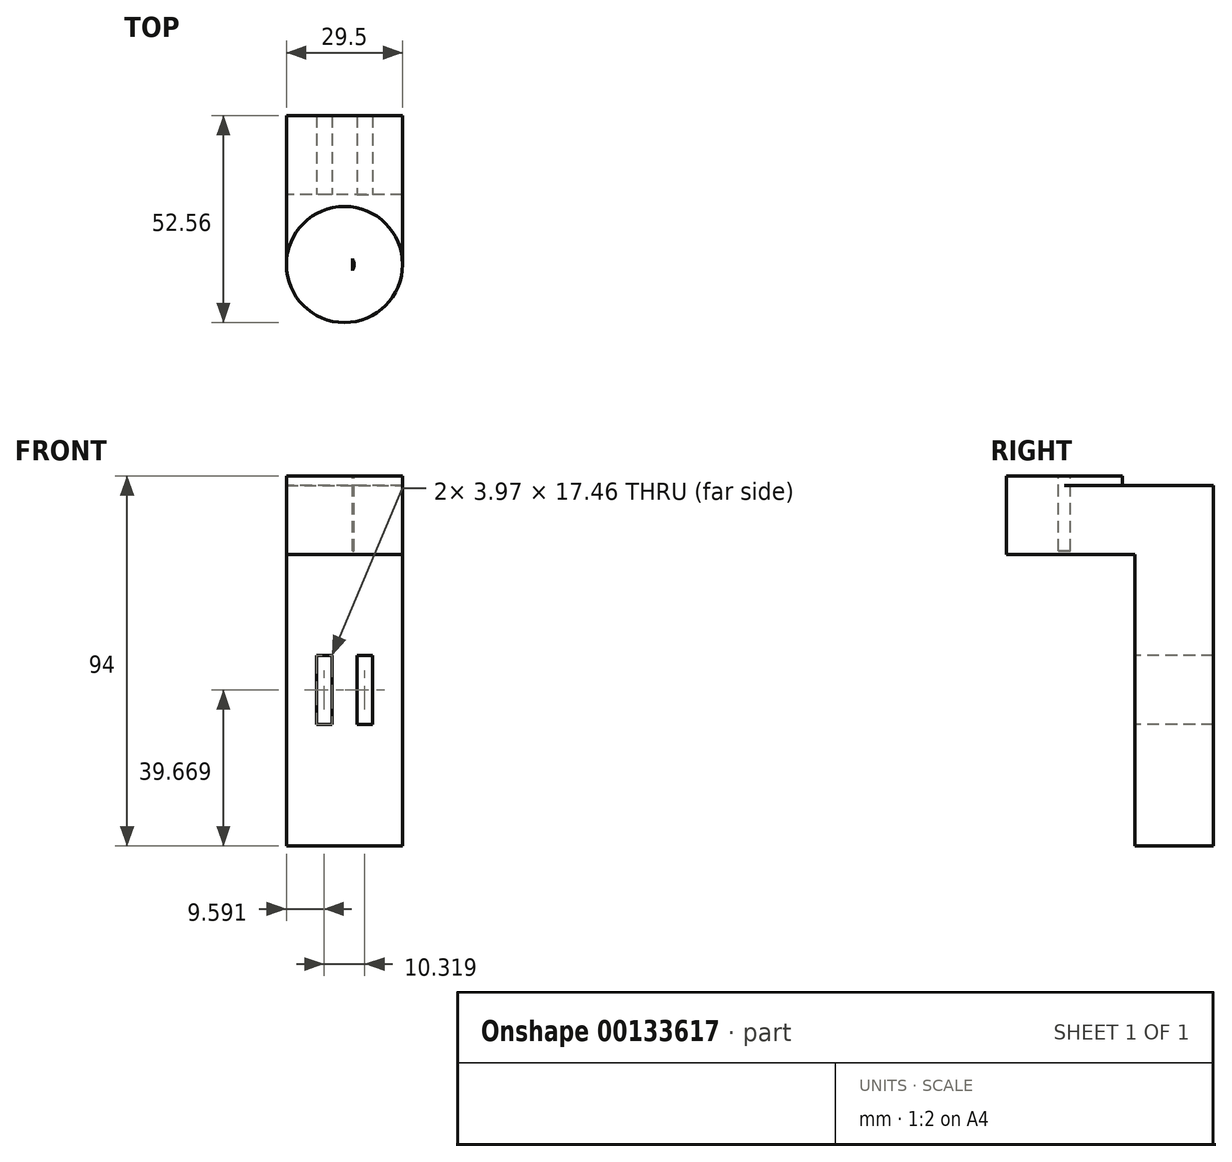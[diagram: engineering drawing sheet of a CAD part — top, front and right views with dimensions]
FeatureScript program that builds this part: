
annotation { "Feature Type Name" : "Feature", "Feature Type Description" : "" }
export const myFeature = defineFeature(function(context is Context, id is Id, definition is map)
    precondition{}
    {
        {
            var Q0;
            Q0=qCreatedBy(makeId("Top.planeOp"),FACE);
            var sketch = newSketch(context, id + "F0", { "sketchPlane" : qUnion([Q0])});
            skCircle(sketch, "E0", {"center": v(0, 0) * mm, "radius": 14.75 * mm});
            skSolve(sketch);
        }
        {
            var Q0;
            Q0=makeQuery(id+"F0.imprint","IMPRINT",FACE,{"disambiguationData":[TD([[makeQuery(id+"F0.imprint","IMPRINT",EDGE,{"derivedFrom":sQuery(id+"F0.wireOp",EDGE,"E0")}),1.0]])]});
            extrude(context, id + "F1", {"entities" : qUnion([Q0]), "depth" : 20 * mm});
        }
        {
            var Q0;
            Q0=makeQuery(id+"F1.opExtrude","CAP_FACE",FACE,{"disambiguationData":[OSD([sQuery(id+"F0.wireOp",EDGE,"E0")])],"isStart":true});
            var sketch = newSketch(context, id + "F2", { "sketchPlane" : qUnion([Q0])});
            skLineSegment(sketch, "E1.bottom", {"start": v(0, -25.5) * mm, "end": v(0, -25.5) * mm});
            skLineSegment(sketch, "E1.top", {"start": v(0, 25.5) * mm, "end": v(0, 25.5) * mm});
            skLineSegment(sketch, "E1.left", {"start": v(0, -25.5) * mm, "end": v(0, 25.5) * mm, "construction": true});
            skLineSegment(sketch, "E1.right", {"start": v(0, -25.5) * mm, "end": v(0, 25.5) * mm});
            skPoint(sketch, "E1.middle", {"position": v(0, 0) * mm});
            skLineSegment(sketch, "E2.bottom", {"start": v(-36.6, 0) * mm, "end": v(36.6, 0) * mm});
            skLineSegment(sketch, "E2.top", {"start": v(-36.6, 0) * mm, "end": v(36.6, 0) * mm, "construction": true});
            skLineSegment(sketch, "E2.left", {"start": v(-36.6, 0) * mm, "end": v(-36.6, 0) * mm});
            skLineSegment(sketch, "E2.right", {"start": v(36.6, 0) * mm, "end": v(36.6, 0) * mm});
            skLineSegment(sketch, "E3", {"start": v(14.75, 0) * mm, "end": v(14.75, -17.8) * mm});
            skLineSegment(sketch, "E4.MirrorCS", {"start": v(-14.75, 0) * mm, "end": v(-14.75, -17.8) * mm});
            skLineSegment(sketch, "E5", {"start": v(14.75, -17.8) * mm, "end": v(14.75, -37.8) * mm});
            skLineSegment(sketch, "E6.MirrorCS", {"start": v(-14.75, -17.8) * mm, "end": v(-14.75, -37.8) * mm});
            skLineSegment(sketch, "E7", {"start": v(14.75, -17.8) * mm, "end": v(-14.75, -17.8) * mm});
            skLineSegment(sketch, "E8", {"start": v(14.75, -37.8) * mm, "end": v(-14.75, -37.8) * mm});
            skSolve(sketch);
        }
        {
            var Q0;
            {var subQ5=sQuery(id+"F2.wireOp",EDGE,"E3");Q0=makeQuery(id+"F2.imprint","IMPRINT",FACE,{"disambiguationData":[TD([[makeQuery(id+"F2.imprint","IMPRINT",EDGE,{"derivedFrom":subQ5}),-1.0]])]});}
            var Q1;
            {var subQ5=sQuery(id+"F2.wireOp",EDGE,"E4.MirrorCS");Q1=makeQuery(id+"F2.imprint","IMPRINT",FACE,{"disambiguationData":[TD([[makeQuery(id+"F2.imprint","IMPRINT",EDGE,{"derivedFrom":subQ5}),1.0]])]});}
            var Q2;
            {var subQ0=sQuery(id+"F2.wireOp",EDGE,"E2.bottom");var subQ1=sQuery(id+"F2.wireOp",EDGE,"E1.right");var subQ2=makeQuery(id+"F2.imprint","INTERSECT",VERTEX,{"derivedFrom":[subQ1,subQ0]});Q2=makeQuery(id+"F2.imprint","IMPRINT",FACE,{"disambiguationData":[TD([[makeQuery(id+"F2.imprint","IMPRINT",EDGE,{"disambiguationData":[TD([[subQ2,1.0]])],"derivedFrom":subQ1}),1.0]])]});}
            var Q3;
            {var subQ0=sQuery(id+"F2.wireOp",EDGE,"E2.bottom");var subQ1=sQuery(id+"F2.wireOp",EDGE,"E1.right");var subQ2=makeQuery(id+"F2.imprint","INTERSECT",VERTEX,{"derivedFrom":[subQ1,subQ0]});Q3=makeQuery(id+"F2.imprint","IMPRINT",FACE,{"disambiguationData":[TD([[makeQuery(id+"F2.imprint","IMPRINT",EDGE,{"disambiguationData":[TD([[subQ2,1.0]])],"derivedFrom":subQ1}),-1.0]])]});}
            var Q4;
            {var subQ1=sQuery(id+"F2.wireOp",EDGE,"E5");Q4=makeQuery(id+"F2.imprint","IMPRINT",FACE,{"disambiguationData":[TD([[makeQuery(id+"F2.imprint","IMPRINT",EDGE,{"derivedFrom":subQ1}),-1.0]])]});}
            extrude(context, id + "F3", {"entities" : qUnion([Q0, Q1, Q2, Q3, Q4]), "operationType" : NewBodyOperationType.ADD, "oppositeDirection" : true, "depth" : 17.54 * mm});
        }
        {
            var Q0;
            {var subQ1=sQuery(id+"F2.wireOp",EDGE,"E5");Q0=makeQuery(id+"F2.imprint","IMPRINT",FACE,{"disambiguationData":[TD([[makeQuery(id+"F2.imprint","IMPRINT",EDGE,{"derivedFrom":subQ1}),-1.0]])]});}
            extrude(context, id + "F4", {"entities" : qUnion([Q0]), "operationType" : NewBodyOperationType.ADD, "depth" : 74 * mm});
        }
        {
            var Q0;
            Q0=makeQuery(id+"F1.opExtrude","CAP_FACE",FACE,{"disambiguationData":[OSD([sQuery(id+"F0.wireOp",EDGE,"E0")])],"isStart":false});
            var sketch = newSketch(context, id + "F5", { "sketchPlane" : qUnion([Q0])});
            skCircle(sketch, "E9", {"center": v(0, 0) * mm, "radius": 2.5 * mm});
            skLineSegment(sketch, "E10.bottom", {"start": v(2, 2.49) * mm, "end": v(3.01, 2.49) * mm});
            skLineSegment(sketch, "E10.top", {"start": v(2, -2.5) * mm, "end": v(3.01, -2.5) * mm});
            skLineSegment(sketch, "E10.left", {"start": v(2, 2.49) * mm, "end": v(2, -2.5) * mm});
            skLineSegment(sketch, "E10.right", {"start": v(3.01, 2.49) * mm, "end": v(3.01, -2.5) * mm});
            skSolve(sketch);
        }
        {
            var Q0;
            {var subQ0=sQuery(id+"F5.wireOp",EDGE,"E10.left");var subQ1=sQuery(id+"F5.wireOp",EDGE,"E9");var subQ2=makeQuery(id+"F5.imprint","INTERSECT",VERTEX,{"disambiguationData":[OD(0.0)],"derivedFrom":[subQ1,subQ0]});Q0=makeQuery(id+"F5.imprint","IMPRINT",FACE,{"disambiguationData":[TD([[makeQuery(id+"F5.imprint","IMPRINT",EDGE,{"disambiguationData":[TD([[subQ2,-1.0]])],"derivedFrom":subQ1}),1.0]])]});}
            extrude(context, id + "F6", {"entities" : qUnion([Q0]), "operationType" : NewBodyOperationType.REMOVE, "oppositeDirection" : true, "depth" : 19 * mm});
        }
        {
            var Q0;
            Q0=makeQuery(id+"F4.opExtrude","SWEPT_FACE",FACE,{"disambiguationData":[OSD([sQuery(id+"F2.wireOp",EDGE,"E7")])]});
            var sketch = newSketch(context, id + "F7", { "sketchPlane" : qUnion([Q0])});
            skLineSegment(sketch, "E11.bottom", {"start": v(0, -86.42) * mm, "end": v(0, -86.42) * mm});
            skLineSegment(sketch, "E11.top", {"start": v(0, 86.42) * mm, "end": v(0, 86.42) * mm});
            skLineSegment(sketch, "E11.left", {"start": v(0, -86.42) * mm, "end": v(0, 86.42) * mm});
            skLineSegment(sketch, "E11.right", {"start": v(0, -86.42) * mm, "end": v(0, 86.42) * mm, "construction": true});
            skPoint(sketch, "E11.middle", {"position": v(0, 0) * mm});
            skPoint(sketch, "E11.cornerSnap0", {"position": v(0, -74) * mm});
            skLineSegment(sketch, "E12.bottom", {"start": v(3.18, -25.6) * mm, "end": v(7.14, -25.6) * mm});
            skLineSegment(sketch, "E12.top", {"start": v(3.18, -43.06) * mm, "end": v(7.14, -43.06) * mm});
            skLineSegment(sketch, "E12.left", {"start": v(3.18, -25.6) * mm, "end": v(3.18, -43.06) * mm});
            skLineSegment(sketch, "E12.right", {"start": v(7.14, -25.6) * mm, "end": v(7.14, -43.06) * mm});
            skPoint(sketch, "E12.middle", {"position": v(5.16, -34.33) * mm});
            skLineSegment(sketch, "E13.MirrorCS", {"start": v(-7.14, -25.6) * mm, "end": v(-7.14, -43.06) * mm});
            skLineSegment(sketch, "E14.MirrorCS", {"start": v(-3.18, -25.6) * mm, "end": v(-3.18, -43.06) * mm});
            skLineSegment(sketch, "E15.MirrorCS", {"start": v(-3.18, -43.06) * mm, "end": v(-7.14, -43.06) * mm});
            skLineSegment(sketch, "E16.MirrorCS", {"start": v(-3.18, -25.6) * mm, "end": v(-7.14, -25.6) * mm});
            skPoint(sketch, "E17.MirrorP", {"position": v(-5.16, -34.33) * mm});
            skSolve(sketch);
        }
        {
            var Q0;
            Q0=qSketchRegion(id+"F7",true);
            extrude(context, id + "F8", {"entities" : qUnion([Q0]), "operationType" : NewBodyOperationType.REMOVE, "endBound" : BoundingType.THROUGH_ALL, "oppositeDirection" : true, "depth" : 25 * mm});
        }
    });
